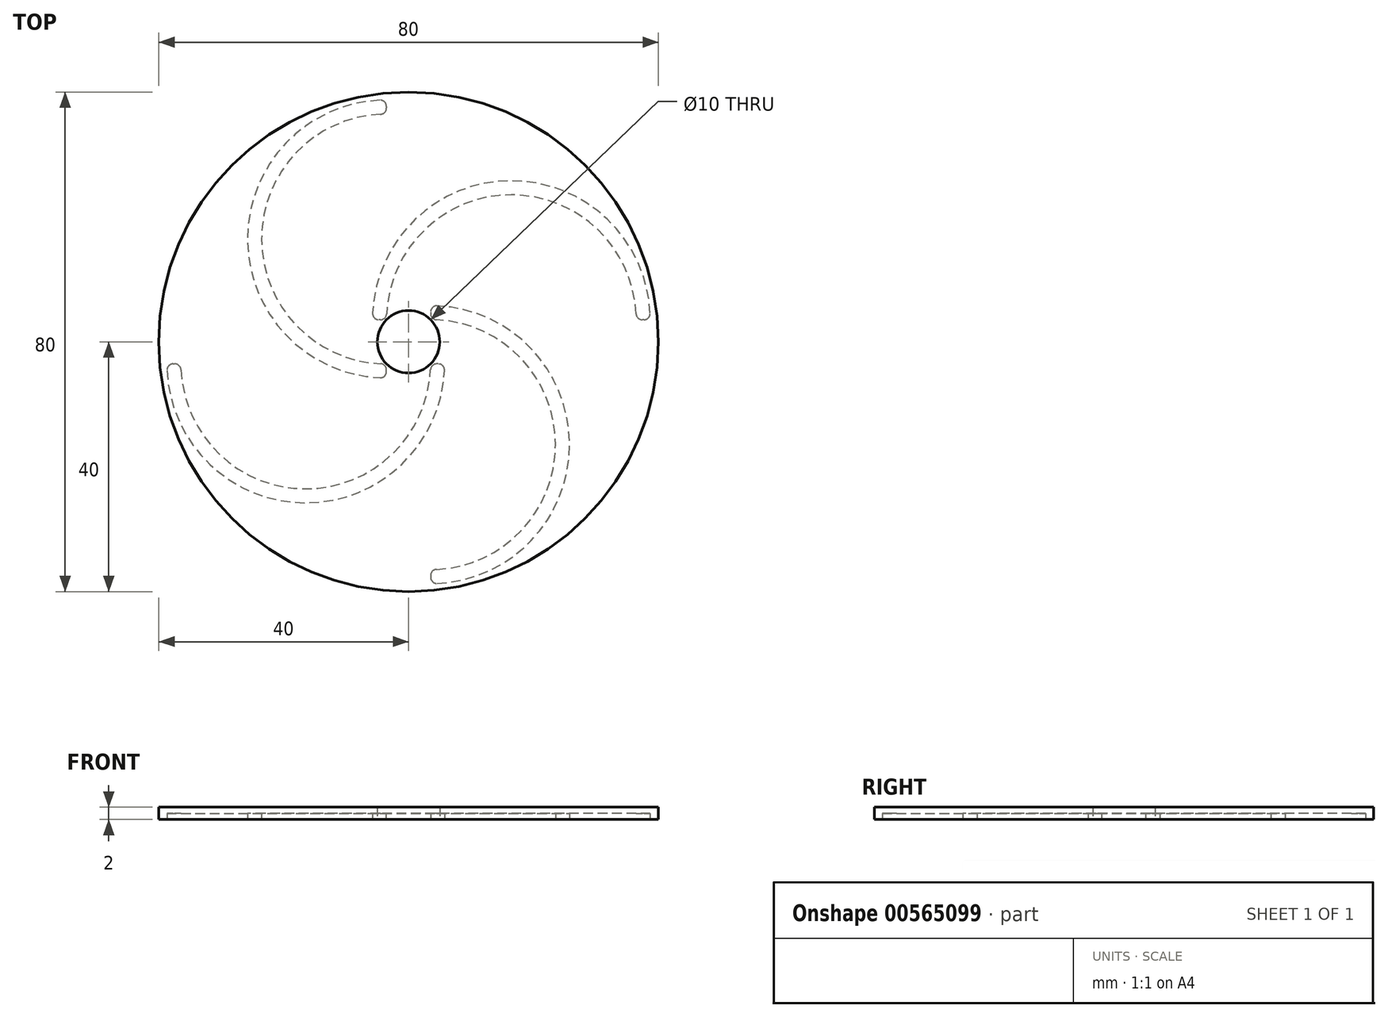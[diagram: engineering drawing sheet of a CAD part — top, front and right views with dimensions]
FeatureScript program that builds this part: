
annotation { "Feature Type Name" : "Feature", "Feature Type Description" : "" }
export const myFeature = defineFeature(function(context is Context, id is Id, definition is map)
    precondition{}
    {
        {
            var Q0;
            Q0=qCreatedBy(makeId("Top.planeOp"),FACE);
            var sketch = newSketch(context, id + "F0", { "sketchPlane" : qUnion([Q0])});
            skCircle(sketch, "E0", {"center": v(0, 0) * mm, "radius": 5 * mm});
            skPoint(sketch, "E1", {"position": v(0, 5) * mm});
            skPoint(sketch, "E2", {"position": v(5, 0) * mm});
            skPoint(sketch, "E3", {"position": v(0, -5) * mm});
            skPoint(sketch, "E4", {"position": v(-5, 0) * mm});
            skLineSegment(sketch, "E5", {"start": v(0, 0) * mm, "end": v(-3.54, -3.54) * mm});
            skLineSegment(sketch, "E6", {"start": v(0, 0) * mm, "end": v(-3.54, 3.54) * mm});
            skLineSegment(sketch, "E7", {"start": v(0, 0) * mm, "end": v(3.54, 3.54) * mm});
            skLineSegment(sketch, "E8", {"start": v(0, 0) * mm, "end": v(3.54, -3.54) * mm});
            skArc(sketch, "E9", {"start": v(3.54, -36.46) * mm, "mid": v(23.54, -16.46) * mm, "end": v(3.54, 3.54) * mm});
            skLineSegment(sketch, "E10", {"start": v(-3.54, -3.54) * mm, "end": v(-3.54, 3.54) * mm});
            skLineSegment(sketch, "E11", {"start": v(3.54, 3.54) * mm, "end": v(3.54, -3.54) * mm});
            skLineSegment(sketch, "E12", {"start": v(3.54, -3.54) * mm, "end": v(-3.54, -3.54) * mm});
            skLineSegment(sketch, "E13", {"start": v(-3.54, 3.54) * mm, "end": v(3.54, 3.54) * mm});
            skArc(sketch, "E14", {"start": v(-3.54, 36.46) * mm, "mid": v(-23.54, 16.46) * mm, "end": v(-3.54, -3.54) * mm});
            skArc(sketch, "E15", {"start": v(36.46, 3.54) * mm, "mid": v(16.46, 23.54) * mm, "end": v(-3.54, 3.54) * mm});
            skArc(sketch, "E16", {"start": v(-36.46, -3.54) * mm, "mid": v(-16.46, -23.54) * mm, "end": v(3.54, -3.54) * mm});
            skArc(sketch, "E17.0", {"start": v(38.71, 3.54) * mm, "mid": v(16.46, 25.79) * mm, "end": v(-5.79, 3.54) * mm});
            skArc(sketch, "E18.0", {"start": v(-3.54, 38.71) * mm, "mid": v(-25.79, 16.46) * mm, "end": v(-3.54, -5.79) * mm});
            skArc(sketch, "E19.0", {"start": v(-38.71, -3.54) * mm, "mid": v(-16.46, -25.79) * mm, "end": v(5.79, -3.54) * mm});
            skArc(sketch, "E20.0", {"start": v(3.54, -38.71) * mm, "mid": v(25.79, -16.46) * mm, "end": v(3.54, 5.79) * mm});
            skLineSegment(sketch, "E21", {"start": v(-3.54, 3.54) * mm, "end": v(-5.79, 3.54) * mm});
            skLineSegment(sketch, "E22", {"start": v(-3.54, -5.79) * mm, "end": v(-3.54, -3.54) * mm});
            skLineSegment(sketch, "E23", {"start": v(5.79, -3.54) * mm, "end": v(3.54, -3.54) * mm});
            skLineSegment(sketch, "E24", {"start": v(3.54, 5.79) * mm, "end": v(3.54, 3.54) * mm});
            skLineSegment(sketch, "E25", {"start": v(38.71, 3.54) * mm, "end": v(36.46, 3.54) * mm});
            skLineSegment(sketch, "E26", {"start": v(-3.54, 38.71) * mm, "end": v(-3.54, 36.46) * mm});
            skLineSegment(sketch, "E27", {"start": v(-38.71, -3.54) * mm, "end": v(-36.46, -3.54) * mm});
            skLineSegment(sketch, "E28", {"start": v(3.54, -36.46) * mm, "end": v(3.54, -38.71) * mm});
            skCircle(sketch, "E29", {"center": v(0, 0) * mm, "radius": 40 * mm});
            skSolve(sketch);
        }
        {
            var Q0;
            {var subQ1=sQuery(id+"F0.wireOp",EDGE,"E9");Q0=makeQuery(id+"F0.imprint","IMPRINT",FACE,{"disambiguationData":[TD([[makeQuery(id+"F0.imprint","IMPRINT",EDGE,{"derivedFrom":subQ1}),1.0]])]});}
            var Q1;
            Q1=makeQuery(id+"F0.imprint","IMPRINT",FACE,{"disambiguationData":[TD([[makeQuery(id+"F0.imprint","IMPRINT",EDGE,{"derivedFrom":sQuery(id+"F0.wireOp",EDGE,"E14")}),-1.0]])]});
            var Q2;
            Q2=makeQuery(id+"F0.imprint","IMPRINT",FACE,{"disambiguationData":[TD([[makeQuery(id+"F0.imprint","IMPRINT",EDGE,{"derivedFrom":sQuery(id+"F0.wireOp",EDGE,"E16")}),-1.0]])]});
            var Q3;
            Q3=makeQuery(id+"F0.imprint","IMPRINT",FACE,{"disambiguationData":[TD([[makeQuery(id+"F0.imprint","IMPRINT",EDGE,{"derivedFrom":sQuery(id+"F0.wireOp",EDGE,"E9")}),-1.0]])]});
            var Q4;
            Q4=makeQuery(id+"F0.imprint","IMPRINT",FACE,{"disambiguationData":[TD([[makeQuery(id+"F0.imprint","IMPRINT",EDGE,{"derivedFrom":sQuery(id+"F0.wireOp",EDGE,"E15")}),-1.0]])]});
            var Q5;
            Q5=makeQuery(id+"F0.imprint","IMPRINT",FACE,{"disambiguationData":[TD([[makeQuery(id+"F0.imprint","IMPRINT",EDGE,{"derivedFrom":sQuery(id+"F0.wireOp",EDGE,"E6")}),-1.0]])]});
            var Q6;
            {var subQ0=sQuery(id+"F0.wireOp",EDGE,"E13");Q6=makeQuery(id+"F0.imprint","IMPRINT",FACE,{"disambiguationData":[TD([[makeQuery(id+"F0.imprint","IMPRINT",EDGE,{"derivedFrom":subQ0}),1.0]])]});}
            var Q7;
            Q7=makeQuery(id+"F0.imprint","IMPRINT",FACE,{"disambiguationData":[TD([[makeQuery(id+"F0.imprint","IMPRINT",EDGE,{"derivedFrom":sQuery(id+"F0.wireOp",EDGE,"E5")}),-1.0]])]});
            var Q8;
            Q8=makeQuery(id+"F0.imprint","IMPRINT",FACE,{"disambiguationData":[TD([[makeQuery(id+"F0.imprint","IMPRINT",EDGE,{"derivedFrom":sQuery(id+"F0.wireOp",EDGE,"E5")}),1.0]])]});
            var Q9;
            Q9=makeQuery(id+"F0.imprint","IMPRINT",FACE,{"disambiguationData":[TD([[makeQuery(id+"F0.imprint","IMPRINT",EDGE,{"derivedFrom":sQuery(id+"F0.wireOp",EDGE,"E7")}),-1.0]])]});
            var Q10;
            {var subQ0=sQuery(id+"F0.wireOp",EDGE,"E11");Q10=makeQuery(id+"F0.imprint","IMPRINT",FACE,{"disambiguationData":[TD([[makeQuery(id+"F0.imprint","IMPRINT",EDGE,{"derivedFrom":subQ0}),1.0]])]});}
            var Q11;
            {var subQ0=sQuery(id+"F0.wireOp",EDGE,"E12");Q11=makeQuery(id+"F0.imprint","IMPRINT",FACE,{"disambiguationData":[TD([[makeQuery(id+"F0.imprint","IMPRINT",EDGE,{"derivedFrom":subQ0}),1.0]])]});}
            var Q12;
            {var subQ0=sQuery(id+"F0.wireOp",EDGE,"E10");Q12=makeQuery(id+"F0.imprint","IMPRINT",FACE,{"disambiguationData":[TD([[makeQuery(id+"F0.imprint","IMPRINT",EDGE,{"derivedFrom":subQ0}),1.0]])]});}
            extrude(context, id + "F1", {"entities" : qUnion([Q0, Q1, Q2, Q3, Q4, Q5, Q6, Q7, Q8, Q9, Q10, Q11, Q12]), "depth" : 2 * mm, "offsetDistance" : 25 * mm});
        }
        {
            var Q0;
            Q0=makeQuery(id+"F0.imprint","IMPRINT",FACE,{"disambiguationData":[TD([[makeQuery(id+"F0.imprint","IMPRINT",EDGE,{"derivedFrom":sQuery(id+"F0.wireOp",EDGE,"E15")}),-1.0]])]});
            var Q1;
            Q1=makeQuery(id+"F0.imprint","IMPRINT",FACE,{"disambiguationData":[TD([[makeQuery(id+"F0.imprint","IMPRINT",EDGE,{"derivedFrom":sQuery(id+"F0.wireOp",EDGE,"E9")}),-1.0]])]});
            var Q2;
            Q2=makeQuery(id+"F0.imprint","IMPRINT",FACE,{"disambiguationData":[TD([[makeQuery(id+"F0.imprint","IMPRINT",EDGE,{"derivedFrom":sQuery(id+"F0.wireOp",EDGE,"E16")}),-1.0]])]});
            var Q3;
            Q3=makeQuery(id+"F0.imprint","IMPRINT",FACE,{"disambiguationData":[TD([[makeQuery(id+"F0.imprint","IMPRINT",EDGE,{"derivedFrom":sQuery(id+"F0.wireOp",EDGE,"E14")}),-1.0]])]});
            extrude(context, id + "F2", {"entities" : qUnion([Q0, Q1, Q2, Q3]), "operationType" : NewBodyOperationType.REMOVE, "depth" : 1 * mm, "offsetDistance" : 25 * mm});
        }
        {
            var Q0;
            Q0=makeQuery(id+"F2.boolean.opBoolean","COPY",EDGE,{"derivedFrom":makeQuery(id+"F2.opExtrude","SWEPT_EDGE",EDGE,{"disambiguationData":[OSD([sQuery(id+"F0.wireOp",EDGE,"E17.0"),sQuery(id+"F0.wireOp",EDGE,"E21")])]})});
            var Q1;
            Q1=makeQuery(id+"F2.boolean.opBoolean","COPY",EDGE,{"derivedFrom":makeQuery(id+"F2.opExtrude","SWEPT_EDGE",EDGE,{"disambiguationData":[OSD([sQuery(id+"F0.wireOp",EDGE,"E0"),sQuery(id+"F0.wireOp",EDGE,"E6"),sQuery(id+"F0.wireOp",EDGE,"E10"),sQuery(id+"F0.wireOp",EDGE,"E13"),sQuery(id+"F0.wireOp",EDGE,"E15"),sQuery(id+"F0.wireOp",EDGE,"E21")])]})});
            var Q2;
            Q2=makeQuery(id+"F2.boolean.opBoolean","COPY",EDGE,{"derivedFrom":makeQuery(id+"F2.opExtrude","SWEPT_EDGE",EDGE,{"disambiguationData":[OSD([sQuery(id+"F0.wireOp",EDGE,"E18.0"),sQuery(id+"F0.wireOp",EDGE,"E22")])]})});
            var Q3;
            Q3=makeQuery(id+"F2.boolean.opBoolean","COPY",EDGE,{"derivedFrom":makeQuery(id+"F2.opExtrude","SWEPT_EDGE",EDGE,{"disambiguationData":[OSD([sQuery(id+"F0.wireOp",EDGE,"E0"),sQuery(id+"F0.wireOp",EDGE,"E5"),sQuery(id+"F0.wireOp",EDGE,"E10"),sQuery(id+"F0.wireOp",EDGE,"E12"),sQuery(id+"F0.wireOp",EDGE,"E14"),sQuery(id+"F0.wireOp",EDGE,"E22")])]})});
            var Q4;
            Q4=makeQuery(id+"F2.boolean.opBoolean","COPY",EDGE,{"derivedFrom":makeQuery(id+"F2.opExtrude","SWEPT_EDGE",EDGE,{"disambiguationData":[OSD([sQuery(id+"F0.wireOp",EDGE,"E19.0"),sQuery(id+"F0.wireOp",EDGE,"E23")])]})});
            var Q5;
            Q5=makeQuery(id+"F2.boolean.opBoolean","COPY",EDGE,{"derivedFrom":makeQuery(id+"F2.opExtrude","SWEPT_EDGE",EDGE,{"disambiguationData":[OSD([sQuery(id+"F0.wireOp",EDGE,"E0"),sQuery(id+"F0.wireOp",EDGE,"E8"),sQuery(id+"F0.wireOp",EDGE,"E11"),sQuery(id+"F0.wireOp",EDGE,"E12"),sQuery(id+"F0.wireOp",EDGE,"E16"),sQuery(id+"F0.wireOp",EDGE,"E23")])]})});
            var Q6;
            Q6=makeQuery(id+"F2.boolean.opBoolean","COPY",EDGE,{"derivedFrom":makeQuery(id+"F2.opExtrude","SWEPT_EDGE",EDGE,{"disambiguationData":[OSD([sQuery(id+"F0.wireOp",EDGE,"E20.0"),sQuery(id+"F0.wireOp",EDGE,"E24")])]})});
            var Q7;
            Q7=makeQuery(id+"F2.boolean.opBoolean","COPY",EDGE,{"derivedFrom":makeQuery(id+"F2.opExtrude","SWEPT_EDGE",EDGE,{"disambiguationData":[OSD([sQuery(id+"F0.wireOp",EDGE,"E0"),sQuery(id+"F0.wireOp",EDGE,"E7"),sQuery(id+"F0.wireOp",EDGE,"E9"),sQuery(id+"F0.wireOp",EDGE,"E11"),sQuery(id+"F0.wireOp",EDGE,"E13"),sQuery(id+"F0.wireOp",EDGE,"E24")])]})});
            var Q8;
            Q8=makeQuery(id+"F2.boolean.opBoolean","COPY",EDGE,{"derivedFrom":makeQuery(id+"F2.opExtrude","SWEPT_EDGE",EDGE,{"disambiguationData":[OSD([sQuery(id+"F0.wireOp",EDGE,"E20.0"),sQuery(id+"F0.wireOp",EDGE,"E28")])]})});
            var Q9;
            Q9=makeQuery(id+"F2.boolean.opBoolean","COPY",EDGE,{"derivedFrom":makeQuery(id+"F2.opExtrude","SWEPT_EDGE",EDGE,{"disambiguationData":[OSD([sQuery(id+"F0.wireOp",EDGE,"E9"),sQuery(id+"F0.wireOp",EDGE,"E28")])]})});
            var Q10;
            Q10=makeQuery(id+"F2.boolean.opBoolean","COPY",EDGE,{"derivedFrom":makeQuery(id+"F2.opExtrude","SWEPT_EDGE",EDGE,{"disambiguationData":[OSD([sQuery(id+"F0.wireOp",EDGE,"E19.0"),sQuery(id+"F0.wireOp",EDGE,"E27")])]})});
            var Q11;
            Q11=makeQuery(id+"F2.boolean.opBoolean","COPY",EDGE,{"derivedFrom":makeQuery(id+"F2.opExtrude","SWEPT_EDGE",EDGE,{"disambiguationData":[OSD([sQuery(id+"F0.wireOp",EDGE,"E16"),sQuery(id+"F0.wireOp",EDGE,"E27")])]})});
            var Q12;
            Q12=makeQuery(id+"F2.boolean.opBoolean","COPY",EDGE,{"derivedFrom":makeQuery(id+"F2.opExtrude","SWEPT_EDGE",EDGE,{"disambiguationData":[OSD([sQuery(id+"F0.wireOp",EDGE,"E18.0"),sQuery(id+"F0.wireOp",EDGE,"E26")])]})});
            var Q13;
            Q13=makeQuery(id+"F2.boolean.opBoolean","COPY",EDGE,{"derivedFrom":makeQuery(id+"F2.opExtrude","SWEPT_EDGE",EDGE,{"disambiguationData":[OSD([sQuery(id+"F0.wireOp",EDGE,"E14"),sQuery(id+"F0.wireOp",EDGE,"E26")])]})});
            var Q14;
            Q14=makeQuery(id+"F2.boolean.opBoolean","COPY",EDGE,{"derivedFrom":makeQuery(id+"F2.opExtrude","SWEPT_EDGE",EDGE,{"disambiguationData":[OSD([sQuery(id+"F0.wireOp",EDGE,"E17.0"),sQuery(id+"F0.wireOp",EDGE,"E25")])]})});
            var Q15;
            Q15=makeQuery(id+"F2.boolean.opBoolean","COPY",EDGE,{"derivedFrom":makeQuery(id+"F2.opExtrude","SWEPT_EDGE",EDGE,{"disambiguationData":[OSD([sQuery(id+"F0.wireOp",EDGE,"E15"),sQuery(id+"F0.wireOp",EDGE,"E25")])]})});
            fillet(context, id + "F3", {"entities" : qUnion([Q0, Q1, Q2, Q3, Q4, Q5, Q6, Q7, Q8, Q9, Q10, Q11, Q12, Q13, Q14, Q15]), "radius" : 1 * mm, "tangentPropagation" : true, "allowEdgeOverflow" : false});
        }
        {
            var Q0;
            Q0=makeQuery(id+"F0.imprint","IMPRINT",FACE,{"disambiguationData":[TD([[makeQuery(id+"F0.imprint","IMPRINT",EDGE,{"derivedFrom":sQuery(id+"F0.wireOp",EDGE,"E7")}),-1.0]])]});
            var Q1;
            {var subQ0=sQuery(id+"F0.wireOp",EDGE,"E11");Q1=makeQuery(id+"F0.imprint","IMPRINT",FACE,{"disambiguationData":[TD([[makeQuery(id+"F0.imprint","IMPRINT",EDGE,{"derivedFrom":subQ0}),1.0]])]});}
            var Q2;
            Q2=makeQuery(id+"F0.imprint","IMPRINT",FACE,{"disambiguationData":[TD([[makeQuery(id+"F0.imprint","IMPRINT",EDGE,{"derivedFrom":sQuery(id+"F0.wireOp",EDGE,"E5")}),1.0]])]});
            var Q3;
            {var subQ0=sQuery(id+"F0.wireOp",EDGE,"E12");Q3=makeQuery(id+"F0.imprint","IMPRINT",FACE,{"disambiguationData":[TD([[makeQuery(id+"F0.imprint","IMPRINT",EDGE,{"derivedFrom":subQ0}),1.0]])]});}
            var Q4;
            Q4=makeQuery(id+"F0.imprint","IMPRINT",FACE,{"disambiguationData":[TD([[makeQuery(id+"F0.imprint","IMPRINT",EDGE,{"derivedFrom":sQuery(id+"F0.wireOp",EDGE,"E5")}),-1.0]])]});
            var Q5;
            Q5=makeQuery(id+"F0.imprint","IMPRINT",FACE,{"disambiguationData":[TD([[makeQuery(id+"F0.imprint","IMPRINT",EDGE,{"derivedFrom":sQuery(id+"F0.wireOp",EDGE,"E6")}),-1.0]])]});
            var Q6;
            {var subQ0=sQuery(id+"F0.wireOp",EDGE,"E13");Q6=makeQuery(id+"F0.imprint","IMPRINT",FACE,{"disambiguationData":[TD([[makeQuery(id+"F0.imprint","IMPRINT",EDGE,{"derivedFrom":subQ0}),1.0]])]});}
            var Q7;
            {var subQ0=sQuery(id+"F0.wireOp",EDGE,"E10");Q7=makeQuery(id+"F0.imprint","IMPRINT",FACE,{"disambiguationData":[TD([[makeQuery(id+"F0.imprint","IMPRINT",EDGE,{"derivedFrom":subQ0}),1.0]])]});}
            extrude(context, id + "F4", {"entities" : qUnion([Q0, Q1, Q2, Q3, Q4, Q5, Q6, Q7]), "operationType" : NewBodyOperationType.REMOVE, "depth" : 25 * mm, "offsetDistance" : 25 * mm});
        }
    });
